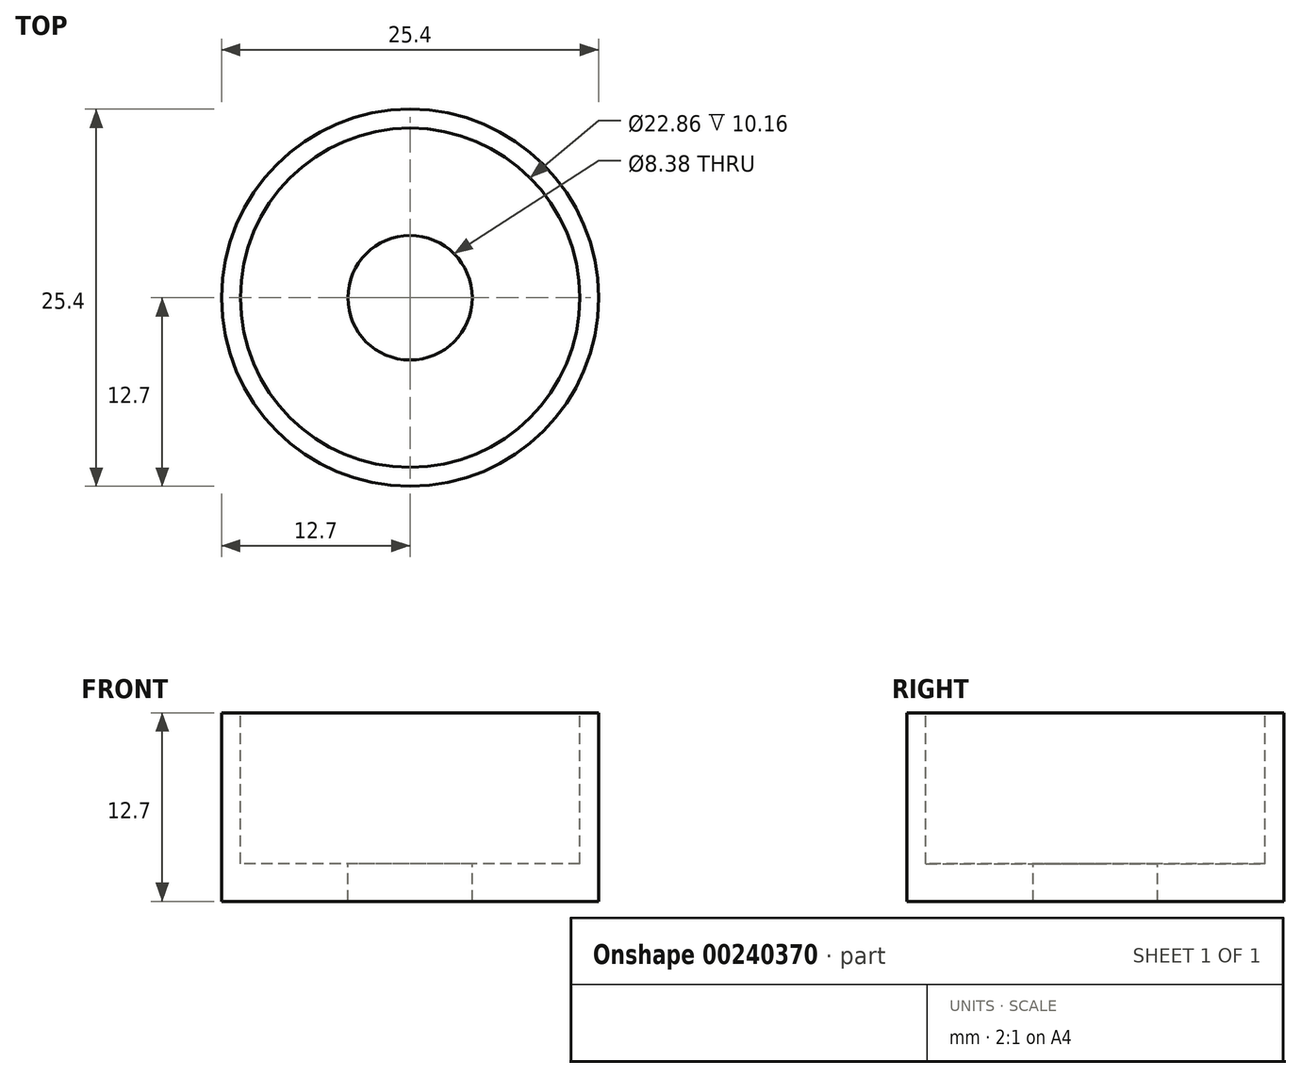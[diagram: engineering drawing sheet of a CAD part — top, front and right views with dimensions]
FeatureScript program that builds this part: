
annotation { "Feature Type Name" : "Feature", "Feature Type Description" : "" }
export const myFeature = defineFeature(function(context is Context, id is Id, definition is map)
    precondition{}
    {
        {
            var Q0;
            Q0=qCreatedBy(makeId("Top.planeOp"),FACE);
            var sketch = newSketch(context, id + "F0", { "sketchPlane" : qUnion([Q0])});
            skCircle(sketch, "E0", {"center": v(0, 0) * mm, "radius": 12.7 * mm});
            skSolve(sketch);
        }
        {
            var Q0;
            Q0 = qSketchRegion(id + "F0", true);
            extrude(context, id + "F1", {"entities" : qUnion([Q0]), "depth" : 12.7 * mm});
        }
        {
            var Q0;
            Q0=makeQuery(id+"F1.opExtrude","CAP_FACE",FACE,{"disambiguationData":[OSD([sQuery(id+"F0.wireOp",EDGE,"E0")])],"isStart":false});
            var sketch = newSketch(context, id + "F2", { "sketchPlane" : qUnion([Q0])});
            skCircle(sketch, "E1", {"center": v(0, 0) * mm, "radius": 11.43 * mm});
            skSolve(sketch);
        }
        {
            var Q0;
            Q0 = qSketchRegion(id + "F2", true);
            extrude(context, id + "F3", {"entities" : qUnion([Q0]), "operationType" : NewBodyOperationType.REMOVE, "oppositeDirection" : true, "depth" : 10.16 * mm});
        }
        {
            var Q0;
            Q0=makeQuery(id+"F3.boolean.opBoolean","COPY",FACE,{"derivedFrom":makeQuery(id+"F3.opExtrude","CAP_FACE",FACE,{"disambiguationData":[OSD([sQuery(id+"F2.wireOp",EDGE,"E1")])],"isStart":false})});
            var sketch = newSketch(context, id + "F4", { "sketchPlane" : qUnion([Q0])});
            skCircle(sketch, "E2", {"center": v(0, 0) * mm, "radius": 4.2 * mm});
            skSolve(sketch);
        }
        {
            var Q0;
            Q0 = qSketchRegion(id + "F4", true);
            extrude(context, id + "F5", {"entities" : qUnion([Q0]), "operationType" : NewBodyOperationType.REMOVE, "endBound" : BoundingType.UP_TO_NEXT, "oppositeDirection" : true, "depth" : 25.4 * mm});
        }
    });
